# Revit family: Klappdeckel mit Schnurauslass
name_source: partatom
category: Generic Models
revit_build: Autodesk Revit 2015 (Build: 20140606_1530(x64)
units: mm (PartAtom-declared; Revit-internal decimal feet)

## types (2) — shared parameters
Diameter = 140 mm  [stored 0.459318 ft]
Diameter 1 = 115 mm  [stored 0.377297 ft]
Height = 40 mm  [stored 0.131234 ft]
Height 1 = 38 mm  [stored 0.124672 ft]
Manufacturer = OBO Bettermann
Radius = 56 mm  [stored 0.183727 ft]
URL = http://www.obo-bettermann.com

## per-type parameters (varying)
| type | GTIN | Manufacturer Art.No. | Material |
| GES R2 9011 | 4012196459599 | 7405084 | OBO PA BLACK |
| GES R2 7011 | 4012196459582 | 7405082 | OBO PA Grey |

note: column(s) folded — value = type name in every type: Article Type

note: [stored X ft] marks values corroborated as IEEE doubles in the binary element streams (Revit-internal decimal feet)

## geometry (parser evidence)
native form markers: Sweep x1
no freeform markers — native parametric forms only
